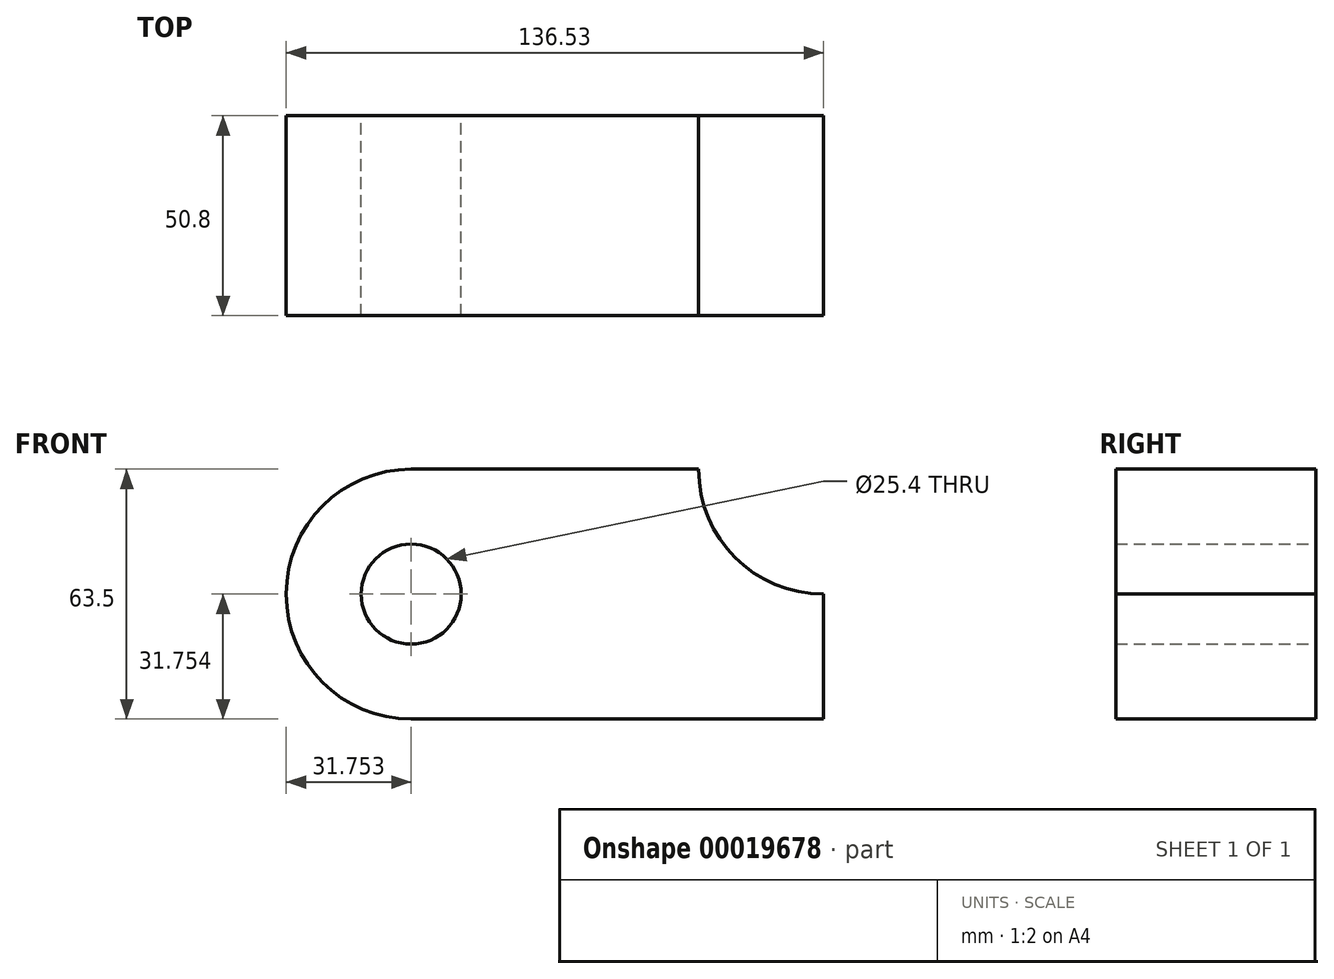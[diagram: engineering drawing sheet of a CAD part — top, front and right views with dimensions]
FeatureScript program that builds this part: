
annotation { "Feature Type Name" : "Feature", "Feature Type Description" : "" }
export const myFeature = defineFeature(function(context is Context, id is Id, definition is map)
    precondition{}
    {
        {
            var Q0;
            Q0=qCreatedBy(makeId("Front.planeOp"),FACE);
            var sketch = newSketch(context, id + "F0", { "sketchPlane" : qUnion([Q0])});
            skLineSegment(sketch, "E0.bottom", {"start": v(-58.35, 34.18) * mm, "end": v(14.68, 34.18) * mm});
            skLineSegment(sketch, "E0.top", {"start": v(-58.35, -29.32) * mm, "end": v(46.43, -29.32) * mm});
            skLineSegment(sketch, "E0.right", {"start": v(46.43, 2.43) * mm, "end": v(46.43, -29.32) * mm});
            skArc(sketch, "E1", {"start": v(-58.35, 34.18) * mm, "mid": v(-90.1, 2.43) * mm, "end": v(-58.35, -29.32) * mm});
            skCircle(sketch, "E2", {"center": v(-58.35, 2.43) * mm, "radius": 12.7 * mm});
            skArc(sketch, "E3", {"start": v(14.68, 34.18) * mm, "mid": v(23.98, 11.73) * mm, "end": v(46.43, 2.43) * mm});
            skSolve(sketch);
        }
        {
            var Q0;
            Q0=makeQuery(id+"F0.imprint","IMPRINT",FACE,{"disambiguationData":[TD([[makeQuery(id+"F0.imprint","IMPRINT",EDGE,{"derivedFrom":sQuery(id+"F0.wireOp",EDGE,"E0.bottom")}),-1.0]])]});
            extrude(context, id + "F1", {"entities" : qUnion([Q0]), "depth" : 50.8 * mm});
        }
    });
